# Revit family: Rørtettingsmansjett_P_I_07987
name_source: partatom
category: Generic Models
revit_build: Autodesk Revit 2018 (Build: 20170223_1515(x64)
units: mm (PartAtom-declared; Revit-internal decimal feet)

## family parameters
Always vertical = No
Can host rebar = No
Cut with Voids When Loaded = No
Part Type = Normal
Room Calculation Point = No
Round Connector Dimension = Use Diameter
Shared = No
Work Plane-Based = Yes

## types (9) — shared parameters
Default Elevation = 1219 mm
URL = https://katalog.haucon.no

## per-type parameters (varying)
| type | Model |
| 50mm | Rørtettingsmansjett 50mm |
| 25mm | Rørtettingsmansjett 25mm |
| 32mm | Rørtettingsmansjett 32mm |
| 75mm | Rørtettingsmansjett 75mm |
| 90mm | Rørtettingsmansjett 90mm |
| 110mm | Rørtettingsmansjett 110mm |
| 125mm | Rørtettingsmansjett 125mm |
| 160mm | Rørtettingsmansjett 160mm |
| 200mm | Rørtettingsmansjett 200mm |

## geometry (parser evidence)
native form markers: Sweep x1
no freeform markers — native parametric forms only
